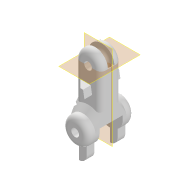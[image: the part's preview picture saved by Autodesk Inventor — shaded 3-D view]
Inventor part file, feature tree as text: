
AUTODESK INVENTOR PART (.ipt)
format: ipt  version: 2020.2 (Build 242310000, 310)  size: 339,968 bytes
history: native  units: mm
features: sketch x9, extrude x5, mirror x3, plane x2, chamfer x2, fillet x2, thread x1, sweep x1
ambient origin geometry x8: Origin, YZ Plane, XZ Plane, XY Plane, X Axis, Y Axis, Z Axis, Center Point
bodies: Solid1 (feature_tree)
feature tree (25):
  extrude  "base"  Depth=10.0mm
  extrude  "joint"  Depth=3.0mm
  plane  "Work Plane1"
  mirror  "Mirror1"
  chamfer  "Chamfer1"  Distance=8.0mm
  extrude  "joint_2"  Depth=10.0mm
  fillet  "Fillet1"  Radius=5.0mm
  plane  "Work Plane2"
  thread  "thread_hole_end"  [1 undecoded]
  extrude  "lock_1"  Depth=9.0mm TaperAngle=0.0deg
  mirror  "Mirror2"
  fillet  "Fillet3"  Radius=2.0mm
  extrude  "lock_2"  Depth=5.25mm
  mirror  "Mirror3"
  chamfer  "Chamfer2"  Distance=25.0mm
  sweep  "Sweep1"
  sketch  "Sketch1"  dims[d0=3.0mm d1=10.0mm]
  sketch  "Sketch2"  dims[d2=20.0mm d3=3.0mm]
  sketch  "Sketch3"  dims[d4=10.0mm d5=8.0mm d6=0.0mm]
  sketch  "Sketch5"  dims[d7=3.0mm d8=10.0mm d9=5.0mm d10=0.0mm d11=2.0mm d12=2.0mm d13=45.0deg]
  sketch  "Sketch6"  dims[d14=10.5mm d15=9.0mm d16=0.0mm d17=2.0mm]
  sketch  "Sketch8"  dims[d21=10.0mm d22=5.25mm]
  sketch  "Sketch9"  dims[d23=3.5mm]
  sketch  "Sketch10"  dims[d24=3.5mm]
  sketch  "Sketch11"  dims[d26=2.5mm d27=25.0mm d28=0.0mm d29=3.5mm d30=2.5mm d31=180.0deg d35=5.0mm d36=3.0mm d37=3.0mm d38=0.0mm d40=3.0mm d41=6.0mm d42=3.0mm d43=13.962634mm d44=3.0mm d45=0.0mm d46=3.0mm d47=2.0mm d48=45.0deg d49=3.5mm d50=10.0mm d52=3.5mm d54=3.0mm d55=0.0mm d56=0.0mm]
note: 1 required parameter value undecoded (feature->parameter linkage not recoverable at this tier; creation-order binding heuristic only, values carry confidence <= 0.55)
